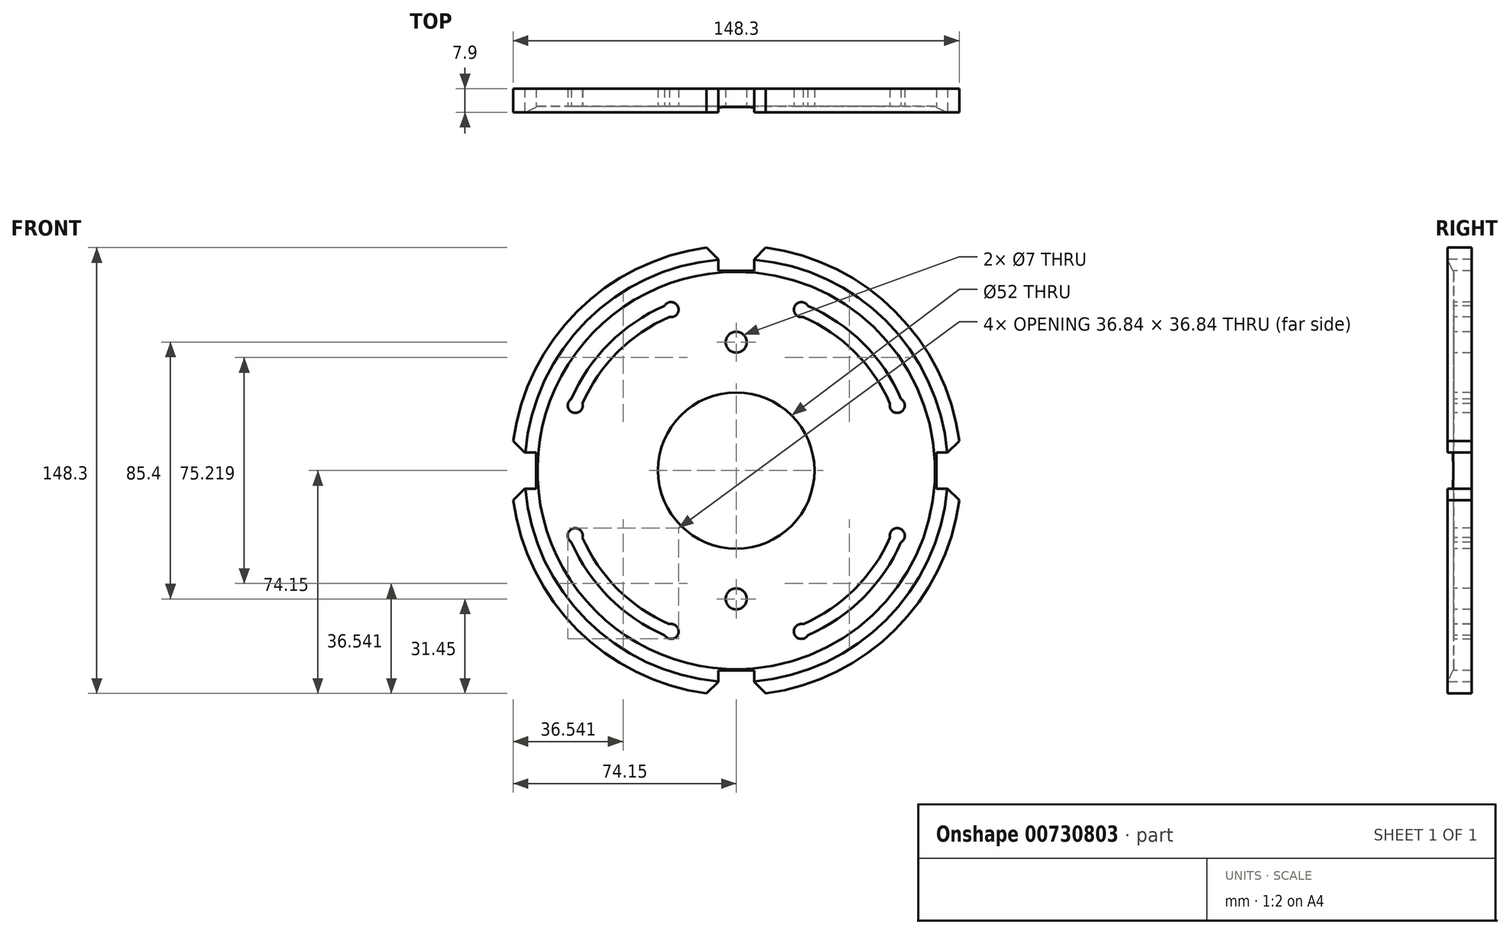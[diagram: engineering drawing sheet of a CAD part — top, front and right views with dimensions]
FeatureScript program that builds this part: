
annotation { "Feature Type Name" : "Feature", "Feature Type Description" : "" }
export const myFeature = defineFeature(function(context is Context, id is Id, definition is map)
    precondition{}
    {
        {
            var Q0;
            Q0=qCreatedBy(makeId("Front.planeOp"),FACE);
            var sketch = newSketch(context, id + "F0", { "sketchPlane" : qUnion([Q0])});
            skCircle(sketch, "E0", {"center": v(0, 0) * mm, "radius": 26 * mm});
            skCircle(sketch, "E1", {"center": v(0, 0) * mm, "radius": 74.8 * mm});
            skArc(sketch, "E2", {"start": v(51.1, 22.27) * mm, "mid": v(39.42, 39.42) * mm, "end": v(22.27, 51.1) * mm});
            skArc(sketch, "E3", {"start": v(23.82, 54.8) * mm, "mid": v(19.35, 54.5) * mm, "end": v(22.27, 51.1) * mm});
            skArc(sketch, "E4", {"start": v(51.1, 22.27) * mm, "mid": v(54.5, 19.35) * mm, "end": v(54.8, 23.82) * mm});
            skArc(sketch, "E5.trimOffspring", {"start": v(54.8, 23.82) * mm, "mid": v(42.25, 42.25) * mm, "end": v(23.82, 54.8) * mm});
            skArc(sketch, "E6.1.0", {"start": v(-23.82, 54.8) * mm, "mid": v(-42.25, 42.25) * mm, "end": v(-54.8, 23.82) * mm});
            skArc(sketch, "E6.1.1", {"start": v(-22.27, 51.1) * mm, "mid": v(-39.42, 39.42) * mm, "end": v(-51.1, 22.27) * mm});
            skArc(sketch, "E6.1.2", {"start": v(-22.27, 51.1) * mm, "mid": v(-19.35, 54.5) * mm, "end": v(-23.82, 54.8) * mm});
            skArc(sketch, "E6.1.3", {"start": v(-54.8, 23.82) * mm, "mid": v(-54.5, 19.35) * mm, "end": v(-51.1, 22.27) * mm});
            skArc(sketch, "E6.2.0", {"start": v(-54.8, -23.82) * mm, "mid": v(-42.25, -42.25) * mm, "end": v(-23.82, -54.8) * mm});
            skArc(sketch, "E6.2.1", {"start": v(-51.1, -22.27) * mm, "mid": v(-39.42, -39.42) * mm, "end": v(-22.27, -51.1) * mm});
            skArc(sketch, "E6.2.2", {"start": v(-51.1, -22.27) * mm, "mid": v(-54.5, -19.35) * mm, "end": v(-54.8, -23.82) * mm});
            skArc(sketch, "E6.2.3", {"start": v(-23.82, -54.8) * mm, "mid": v(-19.35, -54.5) * mm, "end": v(-22.27, -51.1) * mm});
            skArc(sketch, "E6.3.0", {"start": v(23.82, -54.8) * mm, "mid": v(42.25, -42.25) * mm, "end": v(54.8, -23.82) * mm});
            skArc(sketch, "E6.3.1", {"start": v(22.27, -51.1) * mm, "mid": v(39.42, -39.42) * mm, "end": v(51.1, -22.27) * mm});
            skArc(sketch, "E6.3.2", {"start": v(22.27, -51.1) * mm, "mid": v(19.35, -54.5) * mm, "end": v(23.82, -54.8) * mm});
            skArc(sketch, "E6.3.3", {"start": v(54.8, -23.82) * mm, "mid": v(54.5, -19.35) * mm, "end": v(51.1, -22.27) * mm});
            skCircle(sketch, "E7", {"center": v(0, 42.7) * mm, "radius": 3.5 * mm});
            skCircle(sketch, "E8.MirrorC", {"center": v(0, -42.7) * mm, "radius": 3.5 * mm});
            skSolve(sketch);
        }
        {
            var Q0;
            Q0=makeQuery(id+"F0.imprint","IMPRINT",FACE,{"disambiguationData":[TD([[makeQuery(id+"F0.imprint","IMPRINT",EDGE,{"derivedFrom":sQuery(id+"F0.wireOp",EDGE,"NQZRdPuz-UbHe-C8SB-qXKR-qHRhQdRaouHw")}),-1.0]])]});
            var Q1;
            Q1=makeQuery(id+"F0.imprint","IMPRINT",FACE,{"disambiguationData":[TD([[makeQuery(id+"F0.imprint","IMPRINT",EDGE,{"derivedFrom":sQuery(id+"F0.wireOp",EDGE,"E0")}),-1.0]])]});
            var Q2;
            Q2=makeQuery(id+"F0.imprint","IMPRINT",FACE,{"disambiguationData":[TD([[makeQuery(id+"F0.imprint","IMPRINT",EDGE,{"derivedFrom":sQuery(id+"F0.wireOp",EDGE,"E0")}),1.0]])]});
            extrude(context, id + "F1", {"entities" : qUnion([Q0, Q1, Q2]), "oppositeDirection" : true, "depth" : 7.9 * mm, "offsetDistance" : 25 * mm});
        }
        {
            var Q0;
            Q0=makeQuery(id+"F0.imprint","IMPRINT",FACE,{"disambiguationData":[TD([[makeQuery(id+"F0.imprint","IMPRINT",EDGE,{"derivedFrom":sQuery(id+"F0.wireOp",EDGE,"E0")}),1.0]])]});
            var Q1;
            Q1=sQuery(id+"F0.wireOp",EDGE,"E0");
            extrude(context, id + "F2", {"entities" : qUnion([Q0]), "operationType" : NewBodyOperationType.REMOVE, "surfaceEntities" : qUnion([Q1]), "oppositeDirection" : true, "depth" : 7.9 * mm, "offsetDistance" : 25 * mm});
        }
        {
            var Q0;
            Q0=makeQuery(id+"F0.imprint","IMPRINT",FACE,{"disambiguationData":[TD([[makeQuery(id+"F0.imprint","IMPRINT",EDGE,{"derivedFrom":sQuery(id+"F0.wireOp",EDGE,"E0")}),-1.0]])]});
            var sketch = newSketch(context, id + "F3", { "sketchPlane" : qUnion([Q0])});
            skCircle(sketch, "E9", {"center": v(0, 0) * mm, "radius": 66.1 * mm});
            skSolve(sketch);
        }
        {
            var Q0;
            Q0=makeQuery(id+"F3.imprint","IMPRINT",FACE,{"disambiguationData":[TD([[makeQuery(id+"F3.imprint","IMPRINT",EDGE,{"derivedFrom":sQuery(id+"F3.wireOp",EDGE,"E9")}),1.0]])]});
            extrude(context, id + "F4", {"entities" : qUnion([Q0]), "operationType" : NewBodyOperationType.REMOVE, "oppositeDirection" : true, "depth" : 2 * mm, "offsetDistance" : 25 * mm});
        }
        {
            var Q0;
            Q0=qCreatedBy(makeId("Right.planeOp"),FACE);
            var sketch = newSketch(context, id + "F5", { "sketchPlane" : qUnion([Q0])});
            skLineSegment(sketch, "E10", {"start": v(2, 0) * mm, "end": v(2, 66.1) * mm});
            skLineSegment(sketch, "E11", {"start": v(2, 66.1) * mm, "end": v(-1.72, 74.07) * mm});
            skLineSegment(sketch, "E12", {"start": v(-1.72, 74.07) * mm, "end": v(-1.72, 0) * mm});
            skLineSegment(sketch, "E13", {"start": v(-1.72, 0) * mm, "end": v(2, 0) * mm});
            skSolve(sketch);
        }
        {
            var Q0;
            Q0=makeQuery(id+"F5.imprint","IMPRINT",FACE,{"disambiguationData":[TD([[makeQuery(id+"F5.imprint","IMPRINT",EDGE,{"derivedFrom":sQuery(id+"F5.wireOp",EDGE,"E10")}),1.0]])]});
            var Q1;
            Q1=sQuery(id+"F5.wireOp",EDGE,"E13");
            revolve(context, id + "F6", {"operationType" : NewBodyOperationType.REMOVE, "surfaceOperationType" : NewSurfaceOperationType.NEW, "entities" : qUnion([Q0]), "axis" : qUnion([Q1]), "revolveType" : RevolveType.FULL, "oppositeDirection" : true});
        }
        {
            var Q0;
            Q0=makeQuery(id+"F4.boolean.opBoolean","COPY",FACE,{"derivedFrom":makeQuery(id+"F4.opExtrude","CAP_FACE",FACE,{"disambiguationData":[OSD([sQuery(id+"F0.wireOp",EDGE,"E0"),sQuery(id+"F0.wireOp",EDGE,"E2"),sQuery(id+"F0.wireOp",EDGE,"E3"),sQuery(id+"F0.wireOp",EDGE,"E4"),sQuery(id+"F0.wireOp",EDGE,"E5.trimOffspring"),sQuery(id+"F0.wireOp",EDGE,"E6.1.0"),sQuery(id+"F0.wireOp",EDGE,"E6.1.1"),sQuery(id+"F0.wireOp",EDGE,"E6.1.2"),sQuery(id+"F0.wireOp",EDGE,"E6.1.3"),sQuery(id+"F0.wireOp",EDGE,"E6.2.0"),sQuery(id+"F0.wireOp",EDGE,"E6.2.1"),sQuery(id+"F0.wireOp",EDGE,"E6.2.2"),sQuery(id+"F0.wireOp",EDGE,"E6.2.3"),sQuery(id+"F0.wireOp",EDGE,"E6.3.0"),sQuery(id+"F0.wireOp",EDGE,"E6.3.1"),sQuery(id+"F0.wireOp",EDGE,"E6.3.2"),sQuery(id+"F0.wireOp",EDGE,"E6.3.3"),sQuery(id+"F0.wireOp",EDGE,"E7"),sQuery(id+"F0.wireOp",EDGE,"E8.MirrorC"),sQuery(id+"F3.wireOp",EDGE,"E9")])],"isStart":false})});
            var sketch = newSketch(context, id + "F7", { "sketchPlane" : qUnion([Q0])});
            skLineSegment(sketch, "E14", {"start": v(-6, 66.5) * mm, "end": v(-6, 70.3) * mm});
            skLineSegment(sketch, "E15", {"start": v(6, 66.5) * mm, "end": v(6, 70.3) * mm});
            skLineSegment(sketch, "E16", {"start": v(6, 66.5) * mm, "end": v(-6, 66.5) * mm});
            skLineSegment(sketch, "E17", {"start": v(6, 70.3) * mm, "end": v(12.5, 76.8) * mm});
            skLineSegment(sketch, "E18", {"start": v(-6, 70.3) * mm, "end": v(-12.34, 76.64) * mm});
            skLineSegment(sketch, "E19", {"start": v(-12.34, 76.64) * mm, "end": v(12.5, 76.8) * mm});
            skLineSegment(sketch, "E20.1.0", {"start": v(-70.3, 6) * mm, "end": v(-76.8, 12.5) * mm});
            skLineSegment(sketch, "E20.1.1", {"start": v(-76.64, -12.34) * mm, "end": v(-76.8, 12.5) * mm});
            skLineSegment(sketch, "E20.1.2", {"start": v(-70.3, -6) * mm, "end": v(-76.64, -12.34) * mm});
            skLineSegment(sketch, "E20.1.3", {"start": v(-66.5, -6) * mm, "end": v(-70.3, -6) * mm});
            skLineSegment(sketch, "E20.1.4", {"start": v(-66.5, 6) * mm, "end": v(-66.5, -6) * mm});
            skLineSegment(sketch, "E20.1.5", {"start": v(-66.5, 6) * mm, "end": v(-70.3, 6) * mm});
            skLineSegment(sketch, "E20.2.0", {"start": v(-6, -70.3) * mm, "end": v(-12.5, -76.8) * mm});
            skLineSegment(sketch, "E20.2.1", {"start": v(12.34, -76.64) * mm, "end": v(-12.5, -76.8) * mm});
            skLineSegment(sketch, "E20.2.2", {"start": v(6, -70.3) * mm, "end": v(12.34, -76.64) * mm});
            skLineSegment(sketch, "E20.2.3", {"start": v(6, -66.5) * mm, "end": v(6, -70.3) * mm});
            skLineSegment(sketch, "E20.2.4", {"start": v(-6, -66.5) * mm, "end": v(6, -66.5) * mm});
            skLineSegment(sketch, "E20.2.5", {"start": v(-6, -66.5) * mm, "end": v(-6, -70.3) * mm});
            skLineSegment(sketch, "E20.3.0", {"start": v(70.3, -6) * mm, "end": v(76.8, -12.5) * mm});
            skLineSegment(sketch, "E20.3.1", {"start": v(76.64, 12.34) * mm, "end": v(76.8, -12.5) * mm});
            skLineSegment(sketch, "E20.3.2", {"start": v(70.3, 6) * mm, "end": v(76.64, 12.34) * mm});
            skLineSegment(sketch, "E20.3.3", {"start": v(66.5, 6) * mm, "end": v(70.3, 6) * mm});
            skLineSegment(sketch, "E20.3.4", {"start": v(66.5, -6) * mm, "end": v(66.5, 6) * mm});
            skLineSegment(sketch, "E20.3.5", {"start": v(66.5, -6) * mm, "end": v(70.3, -6) * mm});
            skPoint(sketch, "E20.center", {"position": v(0, 0) * mm});
            skSolve(sketch);
        }
        {
            var Q0;
            Q0 = qSketchRegion(id + "F7", true);
            extrude(context, id + "F8", {"entities" : qUnion([Q0]), "operationType" : NewBodyOperationType.REMOVE, "oppositeDirection" : true, "depth" : 5.9 * mm, "offsetDistance" : 25 * mm});
        }
        {
            var Q0;
            Q0=makeQuery(id+"F8.boolean.opBoolean","COPY",FACE,{"derivedFrom":makeQuery(id+"F8.opExtrude","CAP_FACE",FACE,{"disambiguationData":[OSD([sQuery(id+"F7.wireOp",EDGE,"E14"),sQuery(id+"F7.wireOp",EDGE,"E15"),sQuery(id+"F7.wireOp",EDGE,"E16"),sQuery(id+"F7.wireOp",EDGE,"E17"),sQuery(id+"F7.wireOp",EDGE,"E18"),sQuery(id+"F7.wireOp",EDGE,"E19")])],"isStart":true})});
            var Q1;
            Q1=makeQuery(id+"F8.boolean.opBoolean","COPY",FACE,{"derivedFrom":makeQuery(id+"F8.opExtrude","CAP_FACE",FACE,{"disambiguationData":[OSD([sQuery(id+"F7.wireOp",EDGE,"E20.2.0"),sQuery(id+"F7.wireOp",EDGE,"E20.2.1"),sQuery(id+"F7.wireOp",EDGE,"E20.2.2"),sQuery(id+"F7.wireOp",EDGE,"E20.2.3"),sQuery(id+"F7.wireOp",EDGE,"E20.2.4"),sQuery(id+"F7.wireOp",EDGE,"E20.2.5")])],"isStart":true})});
            var Q2;
            Q2=makeQuery(id+"F8.boolean.opBoolean","COPY",FACE,{"derivedFrom":makeQuery(id+"F8.opExtrude","CAP_FACE",FACE,{"disambiguationData":[OSD([sQuery(id+"F7.wireOp",EDGE,"E20.1.0"),sQuery(id+"F7.wireOp",EDGE,"E20.1.1"),sQuery(id+"F7.wireOp",EDGE,"E20.1.2"),sQuery(id+"F7.wireOp",EDGE,"E20.1.3"),sQuery(id+"F7.wireOp",EDGE,"E20.1.4"),sQuery(id+"F7.wireOp",EDGE,"E20.1.5")])],"isStart":true})});
            var Q3;
            Q3=makeQuery(id+"F8.boolean.opBoolean","COPY",FACE,{"derivedFrom":makeQuery(id+"F8.opExtrude","CAP_FACE",FACE,{"disambiguationData":[OSD([sQuery(id+"F7.wireOp",EDGE,"E20.3.0"),sQuery(id+"F7.wireOp",EDGE,"E20.3.1"),sQuery(id+"F7.wireOp",EDGE,"E20.3.2"),sQuery(id+"F7.wireOp",EDGE,"E20.3.3"),sQuery(id+"F7.wireOp",EDGE,"E20.3.4"),sQuery(id+"F7.wireOp",EDGE,"E20.3.5")])],"isStart":true})});
            extrude(context, id + "F9", {"entities" : qUnion([Q0, Q1, Q2, Q3]), "operationType" : NewBodyOperationType.REMOVE, "oppositeDirection" : true, "depth" : 2 * mm, "offsetDistance" : 25 * mm});
        }
    });
